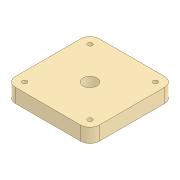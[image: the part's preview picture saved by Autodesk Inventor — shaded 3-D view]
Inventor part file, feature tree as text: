
AUTODESK INVENTOR PART (.ipt)
format: ipt  version: 2020 (Build 240168000, 168)  size: 108,032 bytes
history: native  units: mm
features: mirror x2, other x1, extrude x1, sketch x1
ambient origin geometry x8: Origin, YZ Plane, XZ Plane, XY Plane, X Axis, Y Axis, Z Axis, Center Point
bodies: Body1 (feature_tree)
feature tree (5):
  other  "Sólido1"
  extrude  "Extrusão1"  Depth=36.0mm
  mirror  "Espelhamento1"
  mirror  "Espelhamento2"
  sketch  "Esboço1"  dims[d0=12.0mm d1=36.0mm d2=36.0mm d3=8.0mm d4=4.0mm d5=12.0mm d6=0.0mm d7=8.0mm d8=8.0mm]
